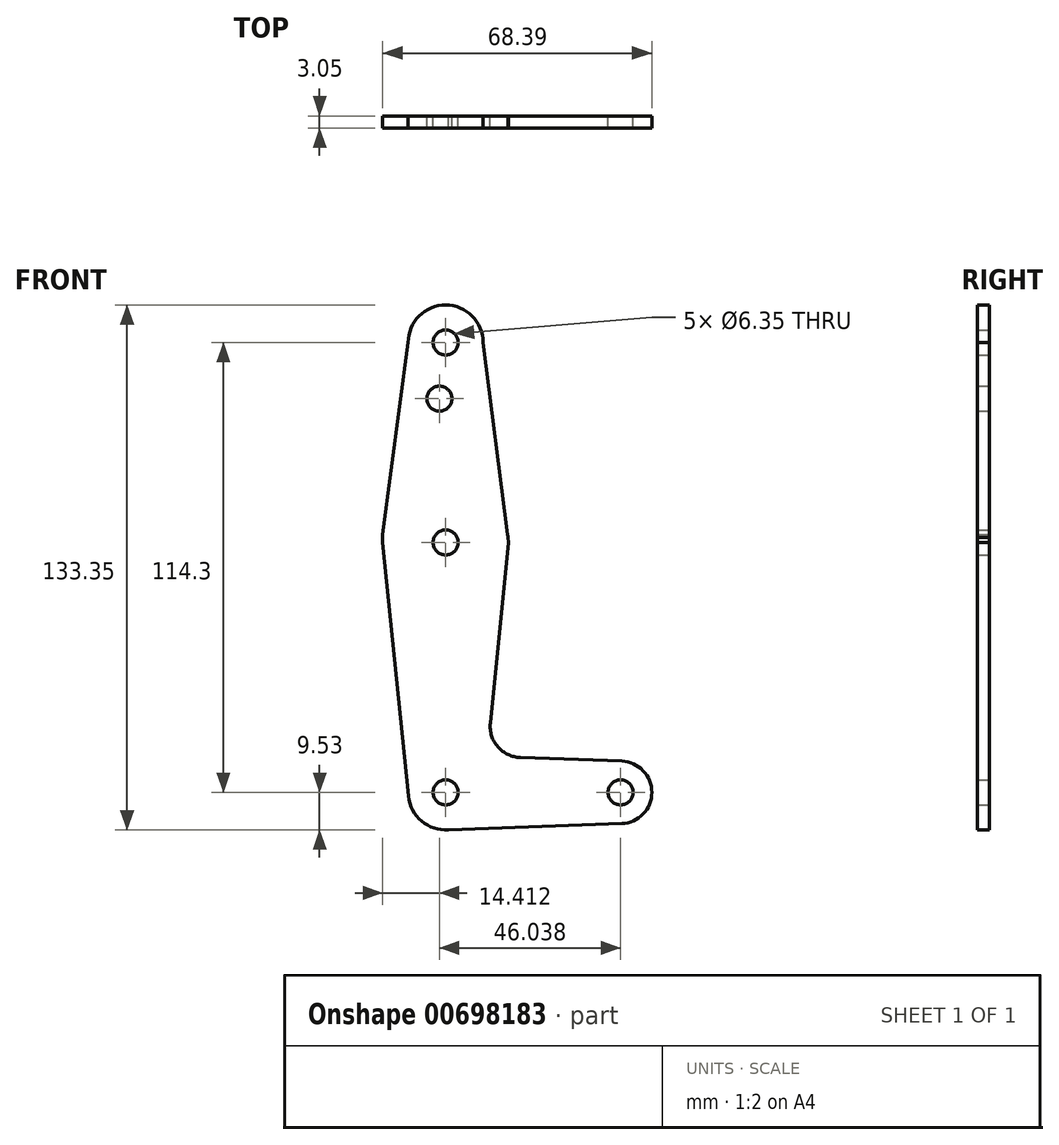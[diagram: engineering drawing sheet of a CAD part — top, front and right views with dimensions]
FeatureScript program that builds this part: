
annotation { "Feature Type Name" : "Feature", "Feature Type Description" : "" }
export const myFeature = defineFeature(function(context is Context, id is Id, definition is map)
    precondition{}
    {
        {
            var Q0;
            Q0=qCreatedBy(makeId("Front.planeOp"),FACE);
            var sketch = newSketch(context, id + "F0", { "sketchPlane" : qUnion([Q0])});
            skLineSegment(sketch, "E0", {"start": v(0, 50.8) * mm, "end": v(0, -63.5) * mm, "construction": true});
            skLineSegment(sketch, "E1", {"start": v(0, -63.5) * mm, "end": v(44.45, -63.5) * mm, "construction": true});
            skCircle(sketch, "E2", {"center": v(0, 50.8) * mm, "radius": 9.53 * mm});
            skCircle(sketch, "E3", {"center": v(0, 0) * mm, "radius": 15.88 * mm});
            skCircle(sketch, "E4", {"center": v(0, -63.5) * mm, "radius": 9.53 * mm});
            skCircle(sketch, "E5", {"center": v(44.45, -63.5) * mm, "radius": 7.94 * mm});
            skLineSegment(sketch, "E6", {"start": v(-16, 0) * mm, "end": v(-9.48, -64.46) * mm});
            skLineSegment(sketch, "E7", {"start": v(-9.48, -64.46) * mm, "end": v(9.48, -64.46) * mm});
            skLineSegment(sketch, "E8", {"start": v(11.34, -45.91) * mm, "end": v(15.95, 0) * mm});
            skLineSegment(sketch, "E9", {"start": v(18.97, -54.65) * mm, "end": v(44.73, -55.57) * mm});
            skLineSegment(sketch, "E10", {"start": v(0, -73.02) * mm, "end": v(44.73, -71.43) * mm});
            skLineSegment(sketch, "E11", {"start": v(9.53, 50.8) * mm, "end": v(15.75, 2) * mm});
            skLineSegment(sketch, "E12", {"start": v(-9.53, 50.8) * mm, "end": v(-16, 2) * mm});
            skLineSegment(sketch, "E13", {"start": v(-16, 2) * mm, "end": v(-16, 0) * mm});
            skLineSegment(sketch, "E14", {"start": v(15.75, 2) * mm, "end": v(15.95, 0) * mm});
            skCircle(sketch, "E15", {"center": v(0, 50.8) * mm, "radius": 3.18 * mm});
            skCircle(sketch, "E16", {"center": v(0, 0) * mm, "radius": 3.18 * mm});
            skCircle(sketch, "E17", {"center": v(0, -63.5) * mm, "radius": 3.18 * mm});
            skCircle(sketch, "E18", {"center": v(44.45, -63.5) * mm, "radius": 3.18 * mm});
            skCircle(sketch, "E19", {"center": v(-1.59, 36.53) * mm, "radius": 3.18 * mm});
            skPoint(sketch, "E20.newPointB", {"position": v(0, -53.97) * mm});
            skArc(sketch, "E20.filletArc", {"start": v(11.34, -45.91) * mm, "mid": v(13.26, -51.93) * mm, "end": v(18.97, -54.65) * mm});
            skSolve(sketch);
        }
        {
            var Q0;
            Q0 = qSketchRegion(id + "F0", true);
            extrude(context, id + "F1", {"entities" : qUnion([Q0]), "depth" : 3.05 * mm, "offsetDistance" : 25.4 * mm});
        }
    });
